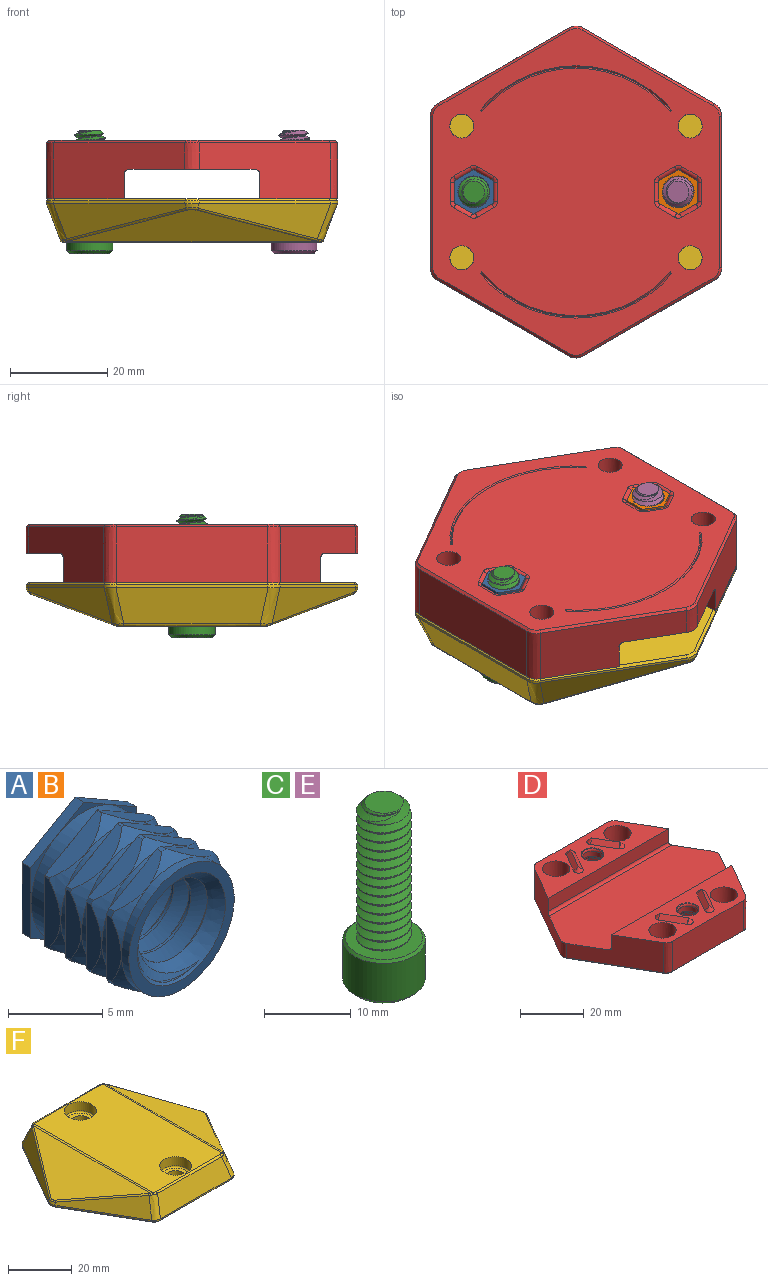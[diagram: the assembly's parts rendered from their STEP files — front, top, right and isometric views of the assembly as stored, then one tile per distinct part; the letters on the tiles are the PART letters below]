
ASSEMBLY  parts=6 mates=4
PART A: 76 faces, bbox 9.1x9x9.2 mm
  f0: cylinder r=3.95mm len=7.9mm, axis (0,1,0), area 24.8mm2, adj f50,f51
  f1: cone r=3.95mm half-angle=35deg, axis (0,1,0), area 9.4mm2, adj f2,f38,f39,f40,f41,f42,f49,f52
  f2: cylinder r=3.95mm len=7.9mm, axis (0,1,0), area 9.2mm2, adj f1,f48
  f3: cone r=3.95mm half-angle=35deg, axis (0,1,0), area 9.3mm2, adj f4,f33,f34,f35,f36,f37,f47,f53
  f4: cylinder r=3.95mm len=7.9mm, axis (0,1,0), area 9.2mm2, adj f3,f46
  f5: cone r=3.95mm half-angle=35deg, axis (0,1,0), area 9.3mm2, adj f6,f28,f29,f30,f31,f32,f45,f54
  f6: cylinder r=3.95mm len=7.9mm, axis (0,1,0), area 9.2mm2, adj f5,f44
  f7: cone r=3.95mm half-angle=35deg, axis (0,1,0), area 9.2mm2, adj f8,f23,f24,f25,f26,f27,f43,f55
  f8: cylinder r=3.95mm len=7.9mm, axis (0,1,0), area 13.4mm2, adj f7,f18
  f9: cylinder r=2.35mm len=6.1mm, axis (0,1,0), area 11.3mm2, adj f10,f11,f20,f21
  f10: cone r=3.3mm half-angle=45deg, axis (0,-1,0), area 14.2mm2, adj f9,f18,f20,f21,f22
  f11: cone r=2.35mm half-angle=45deg, axis (0,1,0), area 14.2mm2, adj f9,f19,f20,f21,f22
  f12: plane 3.96x2.29mm, normal (0.5,0,-0.87), area 3.1mm2, adj f13,f17,f19,f51
  f13: plane 4.58x0.67mm, normal (1,0,0), area 3.1mm2, adj f12,f14,f19,f51
  f14: plane 3.96x2.29mm, normal (0.5,0,0.87), area 3.1mm2, adj f13,f15,f19,f51
  f15: plane 3.96x2.29mm, normal (-0.5,0,0.87), area 3.1mm2, adj f14,f16,f19,f51
  f16: plane 4.58x0.67mm, normal (-1,0,0), area 3.1mm2, adj f15,f17,f19,f51
  f17: plane 3.96x2.29mm, normal (-0.5,0,-0.87), area 3.1mm2, adj f12,f16,f19,f51
  f18: plane 7.9x7.9mm, normal (0,-1,0), area 14.7mm2, adj f8,f10
  f19: plane 9.15x7.92mm, normal (0,1,0), area 20.1mm2, adj f11,f12,f13,f14,f15,f16,f17
  f20: bspline ~8.45x6.35mm, area 90.8mm2, adj f9,f10,f11,f22
  f21: bspline ~8.45x6.35mm, area 91.1mm2, adj f9,f10,f11,f22
  f22: cylinder r=3.17mm len=7.75mm, axis (0,1,0), area 19.3mm2, adj f10,f11,f20,f21
  f23: cone r=4.47mm half-angle=1deg, axis (0,1,0), area 0.1mm2, adj f7,f44,f55,f75
  f24: cone r=4.47mm half-angle=1deg, axis (0,1,0), area 0.1mm2, adj f7,f44,f71,f75
  f25: cone r=4.47mm half-angle=1deg, axis (0,1,0), area 0.1mm2, adj f7,f44,f67,f71
  f26: cone r=4.47mm half-angle=1deg, axis (0,1,0), area 0.1mm2, adj f7,f44,f63,f67
  f27: cone r=4.47mm half-angle=1deg, axis (0,1,0), area 0.1mm2, adj f7,f44,f55,f59
  f28: cone r=4.5mm half-angle=1deg, axis (0,1,0), area 0.1mm2, adj f5,f46,f54,f74
  f29: cone r=4.5mm half-angle=1deg, axis (0,1,0), area 0.1mm2, adj f5,f46,f70,f74
  f30: cone r=4.5mm half-angle=1deg, axis (0,1,0), area 0.1mm2, adj f5,f46,f66,f70
  f31: cone r=4.5mm half-angle=1deg, axis (0,1,0), area 0.1mm2, adj f5,f46,f62,f66
  f32: cone r=4.5mm half-angle=1deg, axis (0,1,0), area 0.1mm2, adj f5,f46,f54,f58
  f33: cone r=4.52mm half-angle=1deg, axis (0,1,0), area 0.1mm2, adj f3,f48,f53,f73
  f34: cone r=4.52mm half-angle=1deg, axis (0,1,0), area 0.1mm2, adj f3,f48,f69,f73
  f35: cone r=4.52mm half-angle=1deg, axis (0,1,0), area 0.1mm2, adj f3,f48,f65,f69
  f36: cone r=4.52mm half-angle=1deg, axis (0,1,0), area 0.1mm2, adj f3,f48,f61,f65
  f37: cone r=4.52mm half-angle=1deg, axis (0,1,0), area 0.1mm2, adj f3,f48,f53,f57
  f38: cone r=4.55mm half-angle=1deg, axis (0,1,0), area 0mm2, adj f1,f50,f52,f72
  f39: cone r=4.55mm half-angle=1deg, axis (0,1,0), area 0mm2, adj f1,f50,f68,f72
  f40: cone r=4.55mm half-angle=1deg, axis (0,1,0), area 0mm2, adj f1,f50,f64,f68
  f41: cone r=4.55mm half-angle=1deg, axis (0,1,0), area 0mm2, adj f1,f50,f60,f64
  f42: cone r=4.55mm half-angle=1deg, axis (0,1,0), area 0mm2, adj f1,f50,f52,f56
  f43: cone r=4.47mm half-angle=1deg, axis (0,1,0), area 0.1mm2, adj f7,f44,f59,f63
  f44: plane 8.95x7.92mm, normal (0,1,0), area 5.3mm2, adj f6,f23,f24,f25,f26,f27,f43,f55
  f45: cone r=4.5mm half-angle=1deg, axis (0,1,0), area 0.1mm2, adj f5,f46,f58,f62
  f46: plane 9.01x7.92mm, normal (0,1,0), area 5.3mm2, adj f4,f28,f29,f30,f31,f32,f45,f54
  f47: cone r=4.52mm half-angle=1deg, axis (0,1,0), area 0.1mm2, adj f3,f48,f57,f61
  f48: plane 9.06x7.93mm, normal (0,1,0), area 5.4mm2, adj f2,f33,f34,f35,f36,f37,f47,f53
  f49: cone r=4.55mm half-angle=1deg, axis (0,1,0), area 0mm2, adj f1,f50,f56,f60
  f50: plane 9.12x7.92mm, normal (0,1,0), area 5.4mm2, adj f0,f38,f39,f40,f41,f42,f49,f52
  f51: plane 9.15x7.92mm, normal (0,-1,0), area 5.4mm2, adj f0,f12,f13,f14,f15,f16,f17
  f52: plane 3.9x2.25mm, normal (-0.5,0,-0.87), area 4.1mm2, adj f1,f38,f42,f50
  f53: plane 3.8x2.2mm, normal (-0.5,0,-0.87), area 3.9mm2, adj f3,f33,f37,f48
  f54: plane 3.7x2.14mm, normal (-0.5,0,-0.87), area 3.7mm2, adj f5,f28,f32,f46
  f55: plane 3.61x2.08mm, normal (-0.5,0,-0.87), area 3.5mm2, adj f7,f23,f27,f44
  f56: plane 4.51x1.21mm, normal (-1,0,0), area 4.1mm2, adj f1,f42,f49,f50
  f57: plane 4.39x1.17mm, normal (-1,0,0), area 3.9mm2, adj f3,f37,f47,f48
  f58: plane 4.28x1.13mm, normal (-1,0,0), area 3.7mm2, adj f5,f32,f45,f46
  f59: plane 4.16x1.1mm, normal (-1,0,0), area 3.5mm2, adj f7,f27,f43,f44
  f60: plane 3.9x2.25mm, normal (-0.5,0,0.87), area 4.1mm2, adj f1,f41,f49,f50
  f61: plane 3.8x2.2mm, normal (-0.5,0,0.87), area 3.9mm2, adj f3,f36,f47,f48
  f62: plane 3.7x2.14mm, normal (-0.5,0,0.87), area 3.7mm2, adj f5,f31,f45,f46
  f63: plane 3.61x2.08mm, normal (-0.5,0,0.87), area 3.5mm2, adj f7,f26,f43,f44
  f64: plane 3.9x2.25mm, normal (0.5,0,0.87), area 4.1mm2, adj f1,f40,f41,f50
  f65: plane 3.8x2.2mm, normal (0.5,0,0.87), area 3.9mm2, adj f3,f35,f36,f48
  f66: plane 3.7x2.14mm, normal (0.5,0,0.87), area 3.7mm2, adj f5,f30,f31,f46
  f67: plane 3.61x2.08mm, normal (0.5,0,0.87), area 3.5mm2, adj f7,f25,f26,f44
  f68: plane 4.51x1.21mm, normal (1,0,0), area 4.1mm2, adj f1,f39,f40,f50
  f69: plane 4.39x1.17mm, normal (1,0,0), area 3.9mm2, adj f3,f34,f35,f48
  f70: plane 4.28x1.13mm, normal (1,0,0), area 3.7mm2, adj f5,f29,f30,f46
  f71: plane 4.16x1.1mm, normal (1,0,0), area 3.5mm2, adj f7,f24,f25,f44
  f72: plane 3.9x2.25mm, normal (0.5,0,-0.87), area 4.1mm2, adj f1,f38,f39,f50
  f73: plane 3.8x2.2mm, normal (0.5,0,-0.87), area 3.9mm2, adj f3,f33,f34,f48
  f74: plane 3.7x2.14mm, normal (0.5,0,-0.87), area 3.7mm2, adj f5,f28,f29,f46
  f75: plane 3.61x2.08mm, normal (0.5,0,-0.87), area 3.5mm2, adj f7,f23,f24,f44
PART B: same geometry as A
PART C: 24 faces, bbox 10.6x10.6x26.9 mm
  f0: cone r=4.76mm half-angle=45deg, axis (0,0,-1), area 13mm2, adj f3,f10
  f1: cone r=4.13mm half-angle=45deg, axis (0,0,1), area 25.1mm2, adj f3,f11
  f2: cone r=2.75mm half-angle=45deg, axis (0,0,-1), area 0.7mm2, adj f11,f22
  f3: cylinder r=4.76mm len=9.53mm, axis (0,0,1), area 161.5mm2, adj f0,f1
  f4: cylinder r=2.35mm len=18.92mm, axis (0,0,-1), area 34.9mm2, adj f5,f8,f9,f10
  f5: cone r=2.22mm half-angle=45deg, axis (0,0,-1), area 12.3mm2, adj f4,f6,f7,f8,f9
  f6: cylinder r=3.17mm len=18.1mm, axis (0,0,1), area 45.1mm2, adj f5,f8,f9,f10
  f7: plane 4.45x4.45mm, normal (0,0,1), area 15.5mm2, adj f5
  f8: bspline ~19.74x7.33mm, area 241.2mm2, adj f4,f5,f6,f10
  f9: bspline ~20.16x7.33mm, area 242mm2, adj f4,f5,f6,f10
  f10: plane 9.39x9.39mm, normal (0,0,1), area 37.8mm2, adj f0,f4,f6,f8,f9
  f11: plane 8.26x8.26mm, normal (0,0,-1), area 29.8mm2, adj f1,f2,f12,f13,f14,f15,f16
  f12: cone r=2.75mm half-angle=45deg, axis (0,0,-1), area 0mm2, adj f11,f18
  f13: cone r=2.75mm half-angle=45deg, axis (0,0,-1), area 0mm2, adj f11,f19
  f14: cone r=2.75mm half-angle=45deg, axis (0,0,-1), area 0mm2, adj f11,f20
  f15: cone r=2.75mm half-angle=45deg, axis (0,0,-1), area 0mm2, adj f11,f21
  f16: cone r=2.75mm half-angle=45deg, axis (0,0,-1), area 0mm2, adj f11,f23
  f17: plane 5.5x4.76mm, normal (0,0,-1), area 19.6mm2, adj f18,f19,f20,f21,f22,f23
  f18: plane 4.61x3.42mm, normal (-0.5,-0.87,0), area 9.1mm2, adj f12,f17,f19,f23
  f19: plane 4.61x3.79mm, normal (-1,0,0), area 9.2mm2, adj f13,f17,f18,f20
  f20: plane 4.61x3.42mm, normal (-0.5,0.87,0), area 9.1mm2, adj f14,f17,f19,f21
  f21: plane 4.61x3.42mm, normal (0.5,0.87,0), area 9.2mm2, adj f15,f17,f20,f22
  f22: plane 3.84x3.02mm, normal (1,0,0), area 9.2mm2, adj f2,f17,f21,f23
  f23: plane 4.61x3.42mm, normal (0.5,-0.87,0), area 9.2mm2, adj f16,f17,f18,f22
PART D: 174 faces, bbox 70.4x61.6x15.7 mm
  f0: plane 53.12x5mm, normal (0,-1,0), area 265.6mm2, adj f1,f5,f11,f49
  f1: plane 27.24x15.83mm, normal (0.87,0.5,0), area 272.2mm2, adj f0,f5,f7,f11,f157,f161,f165
  f2: plane 31.18x11.5mm, normal (0,1,0), area 358.5mm2, adj f5,f160,f161,f162
  f3: cylinder r=3.05mm len=6.1mm, axis (0,0,-1), area 37.8mm2, adj f34,f42,f43,f44,f45,f46,f47,f48
  f4: cylinder r=2.48mm len=4.95mm, axis (0,0,-1), area 62.2mm2, adj f6,f17
  f5: plane 53.32x16.21mm, normal (0,0,1), area 478.5mm2, adj f0,f1,f2,f16,f18,f19,f20,f21
  f6: plane 67.46x59.06mm, normal (0,0,-1), area 2726.4mm2, adj f4,f8,f9,f10,f35,f36,f37,f38
  f7: plane 68.95x26.21mm, normal (0,0,1), area 1605.3mm2, adj f1,f11,f49,f82,f88,f126,f156,f157
  f8: cone r=25.5mm half-angle=45deg, axis (0,0,1), area 15.6mm2, adj f6,f9,f10,f87
  f9: cone r=5mm half-angle=45deg, axis (0,0,1), area 0.1mm2, adj f6,f8,f10
  f10: cone r=26mm half-angle=45deg, axis (0,0,-1), area 15.7mm2, adj f6,f8,f9,f87
  f11: cylinder r=1mm len=54.27mm, axis (1,0,0), area 84.3mm2, adj f0,f1,f7,f49
  f12: plane 6.7x3.4mm, normal (-0.87,-0.5,0), area 26.3mm2, adj f27,f30,f32,f37
  f13: plane 6.7x3.93mm, normal (0,-1,0), area 26.3mm2, adj f29,f32,f35,f70
  f14: plane 6.7x3.93mm, normal (0,1,0), area 26.3mm2, adj f23,f24,f41,f63
  f15: plane 6.7x3.4mm, normal (-0.87,0.5,0), area 26.3mm2, adj f24,f26,f27,f39
  f16: cylinder r=4.25mm len=8.5mm, axis (0,0,-1), area 200.3mm2, adj f5,f22
  f17: plane 7.5x7.5mm, normal (0,0,1), area 24.9mm2, adj f4,f22
  f18: plane 10.38x7.55mm, normal (0.61,0.35,0.71), area 19.6mm2, adj f5,f19,f20,f21
  f19: cone r=1.5mm half-angle=45deg, axis (0,0,-1), area 5mm2, adj f5,f18,f20
  f20: plane 10.38x7.55mm, normal (-0.61,-0.35,0.71), area 19.6mm2, adj f5,f18,f19,f21
  f21: cone r=1.5mm half-angle=45deg, axis (0,0,-1), area 5mm2, adj f5,f18,f20
  f22: torus R=3.75mm, axis (0,0,-1), area 20.1mm2, adj f16,f17
  f23: cylinder r=0.5mm len=3.93mm, axis (1,0,0), area 2.4mm2, adj f14,f25,f48,f64
  f24: cylinder r=0.5mm len=6.7mm, axis (0,0,1), area 3.5mm2, adj f14,f15,f25,f40
  f25: sphere r=0.5mm, area 0.3mm2, adj f23,f24,f26,f47
  f26: cylinder r=0.5mm len=3.63mm, axis (0.5,0.87,0), area 2.4mm2, adj f15,f25,f28,f46
  f27: cylinder r=0.5mm len=6.7mm, axis (0,0,1), area 3.5mm2, adj f12,f15,f28,f38
  f28: sphere r=0.5mm, area 0.3mm2, adj f26,f27,f30,f45
  f29: cylinder r=0.5mm len=3.93mm, axis (-1,0,0), area 2.4mm2, adj f13,f31,f42,f69
  f30: cylinder r=0.5mm len=3.63mm, axis (-0.5,0.87,0), area 2.4mm2, adj f12,f28,f31,f44
  f31: sphere r=0.5mm, area 0.3mm2, adj f29,f30,f32,f43
  f32: cylinder r=0.5mm len=6.7mm, axis (0,0,1), area 3.5mm2, adj f12,f13,f31,f36
  f33: cone r=3.05mm half-angle=45deg, axis (0,0,1), area 6.3mm2, adj f5,f34
  f34: torus R=4.05mm, axis (0,0,-1), area 15.5mm2, adj f3,f33
  f35: cylinder r=1mm len=3.93mm, axis (1,0,0), area 6.2mm2, adj f6,f13,f36,f71
  f36: torus R=1.5mm, axis (0,0,1), area 1.4mm2, adj f6,f32,f35,f37
  f37: cylinder r=1mm len=3.9mm, axis (0.5,-0.87,0), area 6.2mm2, adj f6,f12,f36,f38
  f38: torus R=1.5mm, axis (0,0,1), area 1.4mm2, adj f6,f27,f37,f39
  f39: cylinder r=1mm len=3.9mm, axis (-0.5,-0.87,0), area 6.2mm2, adj f6,f15,f38,f40
  f40: torus R=1.5mm, axis (0,0,1), area 1.4mm2, adj f6,f24,f39,f41
  f41: cylinder r=1mm len=3.93mm, axis (-1,0,0), area 6.2mm2, adj f6,f14,f40,f75
  f42: bspline ~4.2x1.05mm, area 4.2mm2, adj f3,f29,f43,f76
  f43: bspline ~1.02x1mm, area 0.1mm2, adj f3,f31,f42,f44
  f44: bspline ~3.83x2.74mm, area 4.2mm2, adj f3,f30,f43,f45
  f45: bspline ~1.02x0.93mm, area 0.1mm2, adj f3,f28,f44,f46
  f46: bspline ~3.96x2.78mm, area 4.2mm2, adj f3,f26,f45,f47
  f47: bspline ~1.02x1mm, area 0.1mm2, adj f3,f25,f46,f48
  f48: bspline ~4.2x1.05mm, area 4.2mm2, adj f3,f23,f47,f80
  f49: plane 27.24x15.83mm, normal (-0.87,0.5,0), area 272.2mm2, adj f0,f5,f7,f11,f156,f160,f166
  f50: cylinder r=2.48mm len=4.95mm, axis (0,0,-1), area 62.2mm2, adj f6,f57
  f51: cone r=25.5mm half-angle=45deg, axis (0,0,1), area 15.6mm2, adj f6,f52,f53,f128
  f52: cone r=5mm half-angle=45deg, axis (0,0,1), area 0.1mm2, adj f6,f51,f53
  f53: cone r=26mm half-angle=45deg, axis (0,0,-1), area 15.7mm2, adj f6,f51,f52,f128
  f54: plane 6.7x3.4mm, normal (0.87,-0.5,0), area 26.3mm2, adj f66,f68,f70,f72
  f55: plane 6.7x3.4mm, normal (0.87,0.5,0), area 26.3mm2, adj f63,f65,f66,f74
  f56: cylinder r=4.25mm len=8.5mm, axis (0,0,-1), area 200.3mm2, adj f5,f62
  f57: plane 7.5x7.5mm, normal (0,0,1), area 24.9mm2, adj f50,f62
  f58: plane 10.38x7.55mm, normal (-0.61,0.35,0.71), area 19.6mm2, adj f5,f59,f60,f61
  f59: cone r=1.5mm half-angle=45deg, axis (0,0,-1), area 5mm2, adj f5,f58,f60
  f60: plane 10.38x7.55mm, normal (0.61,-0.35,0.71), area 19.6mm2, adj f5,f58,f59,f61
  f61: cone r=1.5mm half-angle=45deg, axis (0,0,-1), area 5mm2, adj f5,f58,f60
  f62: torus R=3.75mm, axis (0,0,-1), area 20.1mm2, adj f56,f57
  f63: cylinder r=0.5mm len=6.7mm, axis (0,0,1), area 3.5mm2, adj f14,f55,f64,f75
  f64: sphere r=0.5mm, area 0.3mm2, adj f23,f63,f65,f80
  f65: cylinder r=0.5mm len=3.63mm, axis (-0.5,0.87,0), area 2.4mm2, adj f55,f64,f67,f79
  f66: cylinder r=0.5mm len=6.7mm, axis (0,0,1), area 3.5mm2, adj f54,f55,f67,f73
  f67: sphere r=0.5mm, area 0.3mm2, adj f65,f66,f68,f78
  f68: cylinder r=0.5mm len=3.63mm, axis (0.5,0.87,0), area 2.4mm2, adj f54,f67,f69,f77
  f69: sphere r=0.5mm, area 0.3mm2, adj f29,f68,f70,f76
  f70: cylinder r=0.5mm len=6.7mm, axis (0,0,1), area 3.5mm2, adj f13,f54,f69,f71
  f71: torus R=1.5mm, axis (0,0,1), area 1.4mm2, adj f6,f35,f70,f72
  f72: cylinder r=1mm len=3.9mm, axis (-0.5,-0.87,0), area 6.2mm2, adj f6,f54,f71,f73
  f73: torus R=1.5mm, axis (0,0,1), area 1.4mm2, adj f6,f66,f72,f74
  f74: cylinder r=1mm len=3.9mm, axis (0.5,-0.87,0), area 6.2mm2, adj f6,f55,f73,f75
  f75: torus R=1.5mm, axis (0,0,1), area 1.4mm2, adj f6,f41,f63,f74
  f76: bspline ~1.02x1mm, area 0.1mm2, adj f3,f42,f69,f77
  f77: bspline ~3.83x2.74mm, area 4.2mm2, adj f3,f68,f76,f78
  f78: bspline ~1.02x0.93mm, area 0.1mm2, adj f3,f67,f77,f79
  f79: bspline ~3.96x2.78mm, area 4.2mm2, adj f3,f65,f78,f80
  f80: bspline ~1.02x1mm, area 0.1mm2, adj f3,f48,f64,f79
  f81: plane 53.12x5mm, normal (0,1,0), area 265.6mm2, adj f82,f86,f88,f126
  f82: plane 27.24x15.83mm, normal (0.87,-0.5,0), area 272.2mm2, adj f7,f81,f86,f88,f157,f159,f169
  f83: plane 31.18x11.5mm, normal (0,-1,0), area 358.5mm2, adj f86,f158,f159,f173
  f84: cylinder r=3.05mm len=6.1mm, axis (0,0,-1), area 37.8mm2, adj f111,f119,f120,f121,f122,f123,f124,f125
  f85: cylinder r=2.48mm len=4.95mm, axis (0,0,-1), area 62.2mm2, adj f6,f94
  f86: plane 53.32x16.21mm, normal (0,0,1), area 478.5mm2, adj f81,f82,f83,f93,f95,f96,f97,f98
  f87: cone r=5mm half-angle=45deg, axis (0,0,1), area 0.1mm2, adj f6,f8,f10
  f88: cylinder r=1mm len=54.27mm, axis (1,0,0), area 84.3mm2, adj f7,f81,f82,f126
  f89: plane 6.7x3.4mm, normal (-0.87,0.5,0), area 26.3mm2, adj f104,f107,f109,f114
  f90: plane 6.7x3.93mm, normal (0,1,0), area 26.3mm2, adj f106,f109,f112,f145
  f91: plane 6.7x3.93mm, normal (0,-1,0), area 26.3mm2, adj f100,f101,f118,f138
  f92: plane 6.7x3.4mm, normal (-0.87,-0.5,0), area 26.3mm2, adj f101,f103,f104,f116
  f93: cylinder r=4.25mm len=8.5mm, axis (0,0,-1), area 200.3mm2, adj f86,f99
  f94: plane 7.5x7.5mm, normal (0,0,1), area 24.9mm2, adj f85,f99
  f95: plane 10.38x7.55mm, normal (0.61,-0.35,0.71), area 19.6mm2, adj f86,f96,f97,f98
  f96: cone r=1.5mm half-angle=45deg, axis (0,0,-1), area 5mm2, adj f86,f95,f97
  f97: plane 10.38x7.55mm, normal (-0.61,0.35,0.71), area 19.6mm2, adj f86,f95,f96,f98
  f98: cone r=1.5mm half-angle=45deg, axis (0,0,-1), area 5mm2, adj f86,f95,f97
  f99: torus R=3.75mm, axis (0,0,-1), area 20.1mm2, adj f93,f94
  f100: cylinder r=0.5mm len=3.93mm, axis (1,0,0), area 2.4mm2, adj f91,f102,f125,f139
  f101: cylinder r=0.5mm len=6.7mm, axis (0,0,1), area 3.5mm2, adj f91,f92,f102,f117
  f102: sphere r=0.5mm, area 0.3mm2, adj f100,f101,f103,f124
  f103: cylinder r=0.5mm len=3.63mm, axis (0.5,-0.87,0), area 2.4mm2, adj f92,f102,f105,f123
  f104: cylinder r=0.5mm len=6.7mm, axis (0,0,1), area 3.5mm2, adj f89,f92,f105,f115
  f105: sphere r=0.5mm, area 0.3mm2, adj f103,f104,f107,f122
  f106: cylinder r=0.5mm len=3.93mm, axis (-1,0,0), area 2.4mm2, adj f90,f108,f119,f144
  f107: cylinder r=0.5mm len=3.63mm, axis (-0.5,-0.87,0), area 2.4mm2, adj f89,f105,f108,f121
  f108: sphere r=0.5mm, area 0.3mm2, adj f106,f107,f109,f120
  f109: cylinder r=0.5mm len=6.7mm, axis (0,0,1), area 3.5mm2, adj f89,f90,f108,f113
  f110: cone r=3.05mm half-angle=45deg, axis (0,0,1), area 6.3mm2, adj f86,f111
  f111: torus R=4.05mm, axis (0,0,-1), area 15.5mm2, adj f84,f110
  f112: cylinder r=1mm len=3.93mm, axis (1,0,0), area 6.2mm2, adj f6,f90,f113,f146
  f113: torus R=1.5mm, axis (0,0,1), area 1.4mm2, adj f6,f109,f112,f114
  f114: cylinder r=1mm len=3.9mm, axis (0.5,0.87,0), area 6.2mm2, adj f6,f89,f113,f115
  f115: torus R=1.5mm, axis (0,0,1), area 1.4mm2, adj f6,f104,f114,f116
  f116: cylinder r=1mm len=3.9mm, axis (-0.5,0.87,0), area 6.2mm2, adj f6,f92,f115,f117
  f117: torus R=1.5mm, axis (0,0,1), area 1.4mm2, adj f6,f101,f116,f118
  f118: cylinder r=1mm len=3.93mm, axis (-1,0,0), area 6.2mm2, adj f6,f91,f117,f150
  f119: bspline ~4.2x1.05mm, area 4.2mm2, adj f84,f106,f120,f151
  f120: bspline ~1.02x1mm, area 0.1mm2, adj f84,f108,f119,f121
  f121: bspline ~3.83x2.74mm, area 4.2mm2, adj f84,f107,f120,f122
  f122: bspline ~1.02x0.93mm, area 0.1mm2, adj f84,f105,f121,f123
  f123: bspline ~3.96x2.78mm, area 4.2mm2, adj f84,f103,f122,f124
  f124: bspline ~1.02x1mm, area 0.1mm2, adj f84,f102,f123,f125
  f125: bspline ~4.2x1.05mm, area 4.2mm2, adj f84,f100,f124,f155
  f126: plane 27.24x15.83mm, normal (-0.87,-0.5,0), area 272.2mm2, adj f7,f81,f86,f88,f156,f158,f170
  f127: cylinder r=2.48mm len=4.95mm, axis (0,0,-1), area 62.2mm2, adj f6,f132
  f128: cone r=5mm half-angle=45deg, axis (0,0,1), area 0.1mm2, adj f6,f51,f53
  f129: plane 6.7x3.4mm, normal (0.87,0.5,0), area 26.3mm2, adj f141,f143,f145,f147
  f130: plane 6.7x3.4mm, normal (0.87,-0.5,0), area 26.3mm2, adj f138,f140,f141,f149
  f131: cylinder r=4.25mm len=8.5mm, axis (0,0,-1), area 200.3mm2, adj f86,f137
  f132: plane 7.5x7.5mm, normal (0,0,1), area 24.9mm2, adj f127,f137
  f133: plane 10.38x7.55mm, normal (-0.61,-0.35,0.71), area 19.6mm2, adj f86,f134,f135,f136
  f134: cone r=1.5mm half-angle=45deg, axis (0,0,-1), area 5mm2, adj f86,f133,f135
  f135: plane 10.38x7.55mm, normal (0.61,0.35,0.71), area 19.6mm2, adj f86,f133,f134,f136
  f136: cone r=1.5mm half-angle=45deg, axis (0,0,-1), area 5mm2, adj f86,f133,f135
  f137: torus R=3.75mm, axis (0,0,-1), area 20.1mm2, adj f131,f132
  f138: cylinder r=0.5mm len=6.7mm, axis (0,0,1), area 3.5mm2, adj f91,f130,f139,f150
  f139: sphere r=0.5mm, area 0.3mm2, adj f100,f138,f140,f155
  f140: cylinder r=0.5mm len=3.63mm, axis (-0.5,-0.87,0), area 2.4mm2, adj f130,f139,f142,f154
  f141: cylinder r=0.5mm len=6.7mm, axis (0,0,1), area 3.5mm2, adj f129,f130,f142,f148
  f142: sphere r=0.5mm, area 0.3mm2, adj f140,f141,f143,f153
  f143: cylinder r=0.5mm len=3.63mm, axis (0.5,-0.87,0), area 2.4mm2, adj f129,f142,f144,f152
  f144: sphere r=0.5mm, area 0.3mm2, adj f106,f143,f145,f151
  f145: cylinder r=0.5mm len=6.7mm, axis (0,0,1), area 3.5mm2, adj f90,f129,f144,f146
  f146: torus R=1.5mm, axis (0,0,1), area 1.4mm2, adj f6,f112,f145,f147
  f147: cylinder r=1mm len=3.9mm, axis (-0.5,0.87,0), area 6.2mm2, adj f6,f129,f146,f148
  f148: torus R=1.5mm, axis (0,0,1), area 1.4mm2, adj f6,f141,f147,f149
  f149: cylinder r=1mm len=3.9mm, axis (0.5,0.87,0), area 6.2mm2, adj f6,f130,f148,f150
  f150: torus R=1.5mm, axis (0,0,1), area 1.4mm2, adj f6,f118,f138,f149
  f151: bspline ~1.02x1mm, area 0.1mm2, adj f84,f119,f144,f152
  f152: bspline ~3.83x2.74mm, area 4.2mm2, adj f84,f143,f151,f153
  f153: bspline ~1.02x0.93mm, area 0.1mm2, adj f84,f142,f152,f154
  f154: bspline ~3.96x2.78mm, area 4.2mm2, adj f84,f140,f153,f155
  f155: bspline ~1.02x1mm, area 0.1mm2, adj f84,f125,f139,f154
  f156: bspline ~6.6x3mm, area 17.4mm2, adj f7,f49,f126,f168
  f157: bspline ~6.6x3mm, area 17.4mm2, adj f1,f7,f82,f167
  f158: bspline ~13.2x2.6mm, area 36.4mm2, adj f83,f86,f126,f172
  f159: bspline ~13.2x2.6mm, area 36.4mm2, adj f82,f83,f86,f171
  f160: bspline ~13.2x2.6mm, area 36.4mm2, adj f2,f5,f49,f164
  f161: bspline ~13.2x2.6mm, area 36.4mm2, adj f1,f2,f5,f163
  f162: plane 31.18x0.5mm, normal (0,0.71,-0.71), area 22mm2, adj f2,f6,f163,f164
  f163: bspline ~2.6x1.75mm, area 2.1mm2, adj f6,f161,f162,f165
  f164: bspline ~2.6x1.75mm, area 2.1mm2, adj f6,f160,f162,f166
  f165: plane 27.25x16.02mm, normal (0.61,0.35,-0.71), area 22mm2, adj f1,f6,f163,f167
  f166: plane 27.25x16.02mm, normal (-0.61,0.35,-0.71), area 22mm2, adj f6,f49,f164,f168
  f167: bspline ~3x0.87mm, area 2.1mm2, adj f6,f157,f165,f169
  f168: bspline ~3x0.87mm, area 2.1mm2, adj f6,f156,f166,f170
  f169: plane 27.25x16.02mm, normal (0.61,-0.35,-0.71), area 22mm2, adj f6,f82,f167,f171
  f170: plane 27.25x16.02mm, normal (-0.61,-0.35,-0.71), area 22mm2, adj f6,f126,f168,f172
  f171: bspline ~2.6x1.75mm, area 2.1mm2, adj f6,f159,f169,f173
  f172: bspline ~2.6x1.75mm, area 2.1mm2, adj f6,f158,f170,f173
  f173: plane 31.18x0.5mm, normal (0,-0.71,-0.71), area 22mm2, adj f6,f83,f171,f172
PART E: same geometry as C
PART F: 104 faces, bbox 68.8x60.6x9.7 mm
  f0: cylinder r=3.05mm len=6.1mm, axis (0,0,-1), area 86.2mm2, adj f10,f103
  f1: plane 27x15.59mm, normal (0.87,0.5,0), area 15.6mm2, adj f11,f43,f51,f78
  f2: plane 31.18x0.5mm, normal (0,1,0), area 15.6mm2, adj f12,f49,f51,f82
  f3: plane 53.01x30.5mm, normal (0,0,1), area 1455.1mm2, adj f9,f29,f52,f53,f59,f61,f63,f64
  f4: plane 67.46x59.06mm, normal (0,0,-1), area 2736.9mm2, adj f74,f75,f76,f77,f78,f79,f80,f81
  f5: plane 8.82x6.04mm, normal (-0.61,-0.35,-0.71), area 21.4mm2, adj f6,f7,f8,f89
  f6: cone r=1.64mm half-angle=45deg, axis (0,0,-1), area 5.9mm2, adj f5,f7,f87
  f7: plane 8.82x6.04mm, normal (0.61,0.35,-0.71), area 21.4mm2, adj f5,f6,f8,f86
  f8: cone r=1.64mm half-angle=45deg, axis (0,0,-1), area 5.9mm2, adj f5,f7,f88
  f9: cylinder r=5mm len=10mm, axis (0,0,1), area 110mm2, adj f3,f13
  f10: plane 9x9mm, normal (0,0,1), area 34.4mm2, adj f0,f13
  f11: plane 27.19x17.29mm, normal (0.81,0.47,0.35), area 137.9mm2, adj f1,f42,f43,f50,f51,f73
  f12: plane 31.4x7.51mm, normal (0,0.94,0.35), area 238.9mm2, adj f2,f48,f49,f50,f51,f66
  f13: torus R=4.5mm, axis (0,0,1), area 23.8mm2, adj f9,f10
  f14: plane 51.71x17.56mm, normal (0.35,0,0.94), area 493.5mm2, adj f53,f67,f69,f71,f72,f73
  f15: plane 27x15.59mm, normal (-0.87,0.5,0), area 15.6mm2, adj f20,f41,f49,f85
  f16: plane 8.82x6.04mm, normal (0.61,-0.35,-0.71), area 21.4mm2, adj f17,f18,f19,f92
  f17: cone r=1.64mm half-angle=45deg, axis (0,0,-1), area 5.9mm2, adj f16,f18,f93
  f18: plane 8.82x6.04mm, normal (-0.61,0.35,-0.71), area 21.4mm2, adj f16,f17,f19,f91
  f19: cone r=1.64mm half-angle=45deg, axis (0,0,-1), area 5.9mm2, adj f16,f18,f90
  f20: plane 27.19x17.29mm, normal (-0.81,0.47,0.35), area 137.9mm2, adj f15,f40,f41,f48,f49,f58
  f21: plane 51.71x17.56mm, normal (-0.35,0,0.94), area 493.5mm2, adj f52,f54,f55,f56,f58,f60
  f22: cylinder r=3.05mm len=6.1mm, axis (0,0,-1), area 86.2mm2, adj f30,f102
  f23: plane 27x15.59mm, normal (0.87,-0.5,0), area 15.6mm2, adj f31,f43,f47,f74
  f24: plane 31.18x0.5mm, normal (0,-1,0), area 15.6mm2, adj f32,f45,f47,f77
  f25: plane 8.82x6.04mm, normal (-0.61,0.35,-0.71), area 21.4mm2, adj f26,f27,f28,f99
  f26: cone r=1.64mm half-angle=45deg, axis (0,0,-1), area 5.9mm2, adj f25,f27,f98
  f27: plane 8.82x6.04mm, normal (0.61,-0.35,-0.71), area 21.4mm2, adj f25,f26,f28,f100
  f28: cone r=1.64mm half-angle=45deg, axis (0,0,-1), area 5.9mm2, adj f25,f27,f101
  f29: cylinder r=5mm len=10mm, axis (0,0,1), area 110mm2, adj f3,f33
  f30: plane 9x9mm, normal (0,0,1), area 34.4mm2, adj f22,f33
  f31: plane 27.19x17.29mm, normal (0.81,-0.47,0.35), area 137.9mm2, adj f23,f42,f43,f46,f47,f69
  f32: plane 31.4x7.51mm, normal (0,-0.94,0.35), area 238.9mm2, adj f24,f44,f45,f46,f47,f61
  f33: torus R=4.5mm, axis (0,0,1), area 23.8mm2, adj f29,f30
  f34: plane 27x15.59mm, normal (-0.87,-0.5,0), area 15.6mm2, adj f39,f41,f45,f81
  f35: plane 8.82x6.04mm, normal (0.61,0.35,-0.71), area 21.4mm2, adj f36,f37,f38,f95
  f36: cone r=1.64mm half-angle=45deg, axis (0,0,-1), area 5.9mm2, adj f35,f37,f94
  f37: plane 8.82x6.04mm, normal (-0.61,-0.35,-0.71), area 21.4mm2, adj f35,f36,f38,f96
  f38: cone r=1.64mm half-angle=45deg, axis (0,0,-1), area 5.9mm2, adj f35,f37,f97
  f39: plane 27.19x17.29mm, normal (-0.81,-0.47,0.35), area 137.9mm2, adj f34,f40,f41,f44,f45,f54
  f40: bspline ~2.81x1.99mm, area 3.2mm2, adj f20,f39,f41,f56
  f41: bspline ~3x1.11mm, area 1.7mm2, adj f15,f20,f34,f39,f40,f83
  f42: bspline ~2.81x1.99mm, area 3.2mm2, adj f11,f31,f43,f71
  f43: bspline ~3x1.11mm, area 1.7mm2, adj f1,f11,f23,f31,f42,f76
  f44: bspline ~9.29x4.83mm, area 23.7mm2, adj f32,f39,f45,f55,f57,f59
  f45: bspline ~2.6x1.5mm, area 1.7mm2, adj f24,f32,f34,f39,f44,f79
  f46: bspline ~9.29x4.83mm, area 23.7mm2, adj f31,f32,f47,f63,f65,f67
  f47: bspline ~2.6x1.5mm, area 1.7mm2, adj f23,f24,f31,f32,f46,f75
  f48: bspline ~9.29x4.83mm, area 23.7mm2, adj f12,f20,f49,f60,f62,f64
  f49: bspline ~2.6x1.5mm, area 1.7mm2, adj f2,f12,f15,f20,f48,f84
  f50: bspline ~9.29x4.83mm, area 23.7mm2, adj f11,f12,f51,f68,f70,f72
  f51: bspline ~2.6x1.5mm, area 1.7mm2, adj f1,f2,f11,f12,f50,f80
  f52: bspline ~58.81x0.7mm, area 37.4mm2, adj f3,f21,f57,f62
  f53: bspline ~58.81x0.7mm, area 37.4mm2, adj f3,f14,f65,f70
  f54: bspline ~24.79x17.2mm, area 20.8mm2, adj f21,f39,f55,f56
  f55: bspline ~0.8x0.63mm, area 0.4mm2, adj f21,f44,f54,f57
  f56: bspline ~3.1x1.01mm, area 1.7mm2, adj f21,f40,f54,f58
  f57: bspline ~0.97x0.92mm, area 0.6mm2, adj f44,f52,f55,f59
  f58: bspline ~24.79x17.2mm, area 20.8mm2, adj f20,f21,f56,f60
  f59: bspline ~1.53x1.01mm, area 1.3mm2, adj f3,f44,f57,f61
  f60: bspline ~0.78x0.62mm, area 0.4mm2, adj f21,f48,f58,f62
  f61: bspline ~28.14x0.7mm, area 25.9mm2, adj f3,f32,f59,f63
  f62: bspline ~1.13x1.05mm, area 0.6mm2, adj f48,f52,f60,f64
  f63: bspline ~1.53x1.01mm, area 1.3mm2, adj f3,f46,f61,f65
  f64: bspline ~1.9x1.01mm, area 1.3mm2, adj f3,f48,f62,f66
  f65: bspline ~0.97x0.92mm, area 0.6mm2, adj f46,f53,f63,f67
  f66: bspline ~39.98x0.7mm, area 25.9mm2, adj f3,f12,f64,f68
  f67: bspline ~0.78x0.62mm, area 0.4mm2, adj f14,f46,f65,f69
  f68: bspline ~2.1x1.38mm, area 1.3mm2, adj f3,f50,f66,f70
  f69: bspline ~24.79x17.2mm, area 20.8mm2, adj f14,f31,f67,f71
  f70: bspline ~0.99x0.94mm, area 0.7mm2, adj f50,f53,f68,f72
  f71: bspline ~2.81x0.81mm, area 1.7mm2, adj f14,f42,f69,f73
  f72: bspline ~1.21x0.91mm, area 0.3mm2, adj f14,f50,f70,f73
  f73: bspline ~26.43x18.33mm, area 20.8mm2, adj f11,f14,f71,f72
  f74: plane 27.25x16.02mm, normal (0.61,-0.35,-0.71), area 22mm2, adj f4,f23,f75,f76
  f75: bspline ~2.6x1.75mm, area 2.1mm2, adj f4,f47,f74,f77
  f76: bspline ~3x0.87mm, area 2.1mm2, adj f4,f43,f74,f78
  f77: plane 31.18x0.5mm, normal (0,-0.71,-0.71), area 22mm2, adj f4,f24,f75,f79
  f78: plane 27.25x16.02mm, normal (0.61,0.35,-0.71), area 22mm2, adj f1,f4,f76,f80
  f79: bspline ~2.6x1.75mm, area 2.1mm2, adj f4,f45,f77,f81
  f80: bspline ~2.6x1.75mm, area 2.1mm2, adj f4,f51,f78,f82
  f81: plane 27.25x16.02mm, normal (-0.61,-0.35,-0.71), area 22mm2, adj f4,f34,f79,f83
  f82: plane 31.18x0.5mm, normal (0,0.71,-0.71), area 22mm2, adj f2,f4,f80,f84
  f83: bspline ~3x0.87mm, area 2.1mm2, adj f4,f41,f81,f85
  f84: bspline ~2.6x1.75mm, area 2.1mm2, adj f4,f49,f82,f85
  f85: plane 27.25x16.02mm, normal (-0.61,0.35,-0.71), area 22mm2, adj f4,f15,f83,f84
  f86: plane 8.18x4.93mm, normal (0.33,0.19,-0.92), area 3.5mm2, adj f4,f7,f87,f88
  f87: cone r=1.64mm half-angle=67.5deg, axis (0,0,-1), area 2.2mm2, adj f4,f6,f86,f89
  f88: cone r=1.64mm half-angle=67.5deg, axis (0,0,-1), area 2.2mm2, adj f4,f8,f86,f89
  f89: plane 8.18x4.93mm, normal (-0.33,-0.19,-0.92), area 3.5mm2, adj f4,f5,f87,f88
  f90: cone r=1.99mm half-angle=67.5deg, axis (0,0,-1), area 2.2mm2, adj f4,f19,f91,f92
  f91: plane 8.18x4.93mm, normal (-0.33,0.19,-0.92), area 3.5mm2, adj f4,f18,f90,f93
  f92: plane 8.18x4.93mm, normal (0.33,-0.19,-0.92), area 3.5mm2, adj f4,f16,f90,f93
  f93: cone r=1.99mm half-angle=67.5deg, axis (0,0,-1), area 2.2mm2, adj f4,f17,f91,f92
  f94: cone r=1.64mm half-angle=67.5deg, axis (0,0,-1), area 2.2mm2, adj f4,f36,f95,f96
  f95: plane 8.18x4.93mm, normal (0.33,0.19,-0.92), area 3.5mm2, adj f4,f35,f94,f97
  f96: plane 8.18x4.93mm, normal (-0.33,-0.19,-0.92), area 3.5mm2, adj f4,f37,f94,f97
  f97: cone r=1.64mm half-angle=67.5deg, axis (0,0,-1), area 2.2mm2, adj f4,f38,f95,f96
  f98: cone r=1.99mm half-angle=67.5deg, axis (0,0,-1), area 2.2mm2, adj f4,f26,f99,f100
  f99: plane 8.18x4.93mm, normal (-0.33,0.19,-0.92), area 3.5mm2, adj f4,f25,f98,f101
  f100: plane 8.18x4.93mm, normal (0.33,-0.19,-0.92), area 3.5mm2, adj f4,f27,f98,f101
  f101: cone r=1.99mm half-angle=67.5deg, axis (0,0,-1), area 2.2mm2, adj f4,f28,f99,f100
  f102: cone r=3.05mm half-angle=45deg, axis (0,0,-1), area 14.7mm2, adj f4,f22
  f103: cone r=3.55mm half-angle=45deg, axis (0,0,-1), area 14.7mm2, adj f0,f4
PLACE A rot(axis=(0,0.71,0.71),180deg) t=(-27.18,52.13,-20.13)mm
PLACE B rot(axis=(0,0.71,0.71),180deg) t=(14.92,52.13,-20.13)mm
PLACE C t=(-27.18,52.13,-18.08)mm
PLACE D rot(axis=(0.71,-0.71,0),180deg) t=(-6.13,52.13,-20.13)mm fixed
PLACE E t=(14.92,52.13,-18.08)mm
PLACE F rot(axis=(0.71,-0.71,0),180deg) t=(-6.13,52.13,-20.13)mm
MATE fastened D.f3 <-> A.f9  axis (0,0,1) through (-27.18,52.13,-20.13)mm
MATE fastened F.f0 <-> C.f0  axis (0,0,-1) through (-27.18,52.13,-37.13)mm
MATE fastened F.f29 <-> E.f0  axis (0,0,-1) through (14.92,52.13,-37.13)mm
MATE fastened B.f9 <-> D.f84  axis (0,0,1) through (14.92,52.13,-20.13)mm
